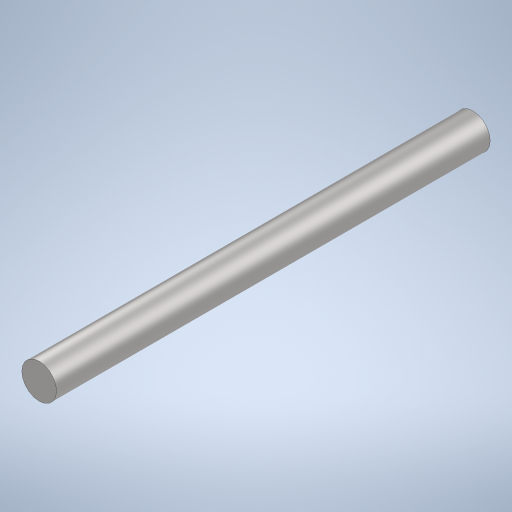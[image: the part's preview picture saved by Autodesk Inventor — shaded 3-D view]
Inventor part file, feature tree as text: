
AUTODESK INVENTOR PART (.ipt)
format: ipt  version: 2023.2 (Build 272271000, 271)  size: 245,248 bytes
history: native  units: mm
features: extrude x1, sketch x1
ambient origin geometry x8: Origin, YZ Plane, XZ Plane, XY Plane, X Axis, Y Axis, Z Axis, Center Point
bodies: Solid1 (feature_tree)
feature tree (2):
  extrude  "Extrusion1"  Depth=100.0mm TaperAngle=0.0deg
  sketch  "Sketch1"  dims[d0=8.0mm d1=100.0mm d2=0.0mm]
